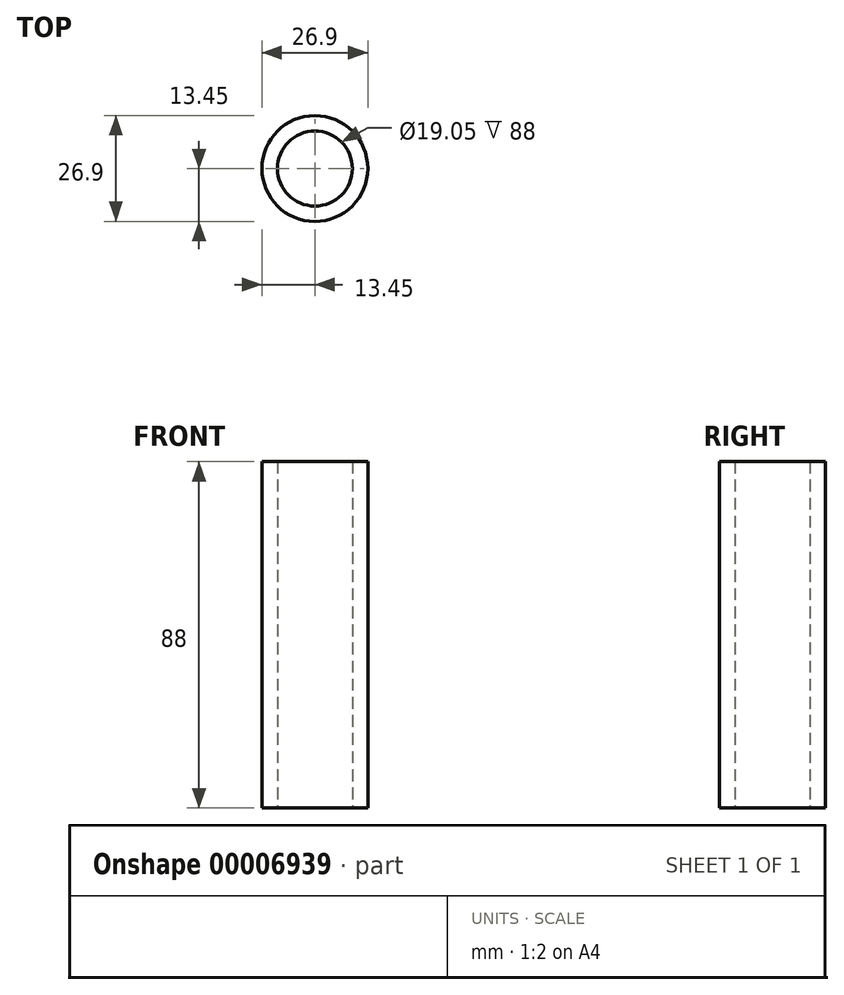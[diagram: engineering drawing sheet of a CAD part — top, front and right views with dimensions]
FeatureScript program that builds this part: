
annotation { "Feature Type Name" : "Feature", "Feature Type Description" : "" }
export const myFeature = defineFeature(function(context is Context, id is Id, definition is map)
    precondition{}
    {
        {
            var Q0;
            Q0=qCreatedBy(makeId("Top.planeOp"),FACE);
            var sketch = newSketch(context, id + "F0", { "sketchPlane" : qUnion([Q0])});
            skCircle(sketch, "E0", {"center": v(0, 0) * mm, "radius": 13.45 * mm});
            skCircle(sketch, "E1", {"center": v(0, 0) * mm, "radius": 9.53 * mm});
            skSolve(sketch);
        }
        {
            var Q0;
            Q0=makeQuery(id+"F0.imprint","IMPRINT",FACE,{"disambiguationData":[TD([[makeQuery(id+"F0.imprint","IMPRINT",EDGE,{"derivedFrom":sQuery(id+"F0.wireOp",EDGE,"E0")}),1.0]])]});
            extrude(context, id + "F1", {"entities" : qUnion([Q0]), "depth" : (88) * mm});
        }
    });
